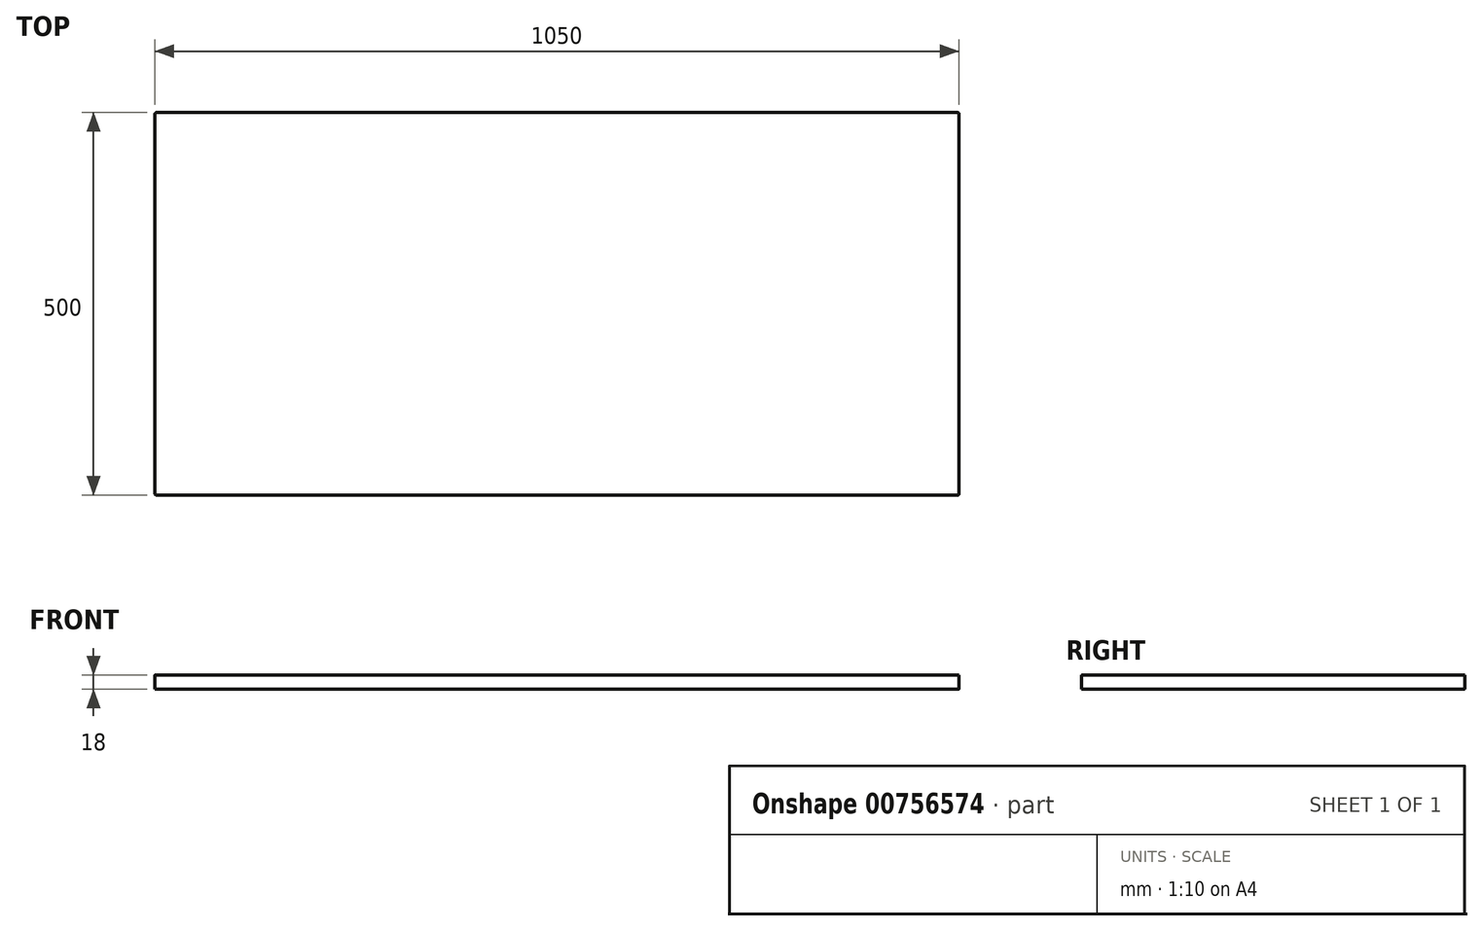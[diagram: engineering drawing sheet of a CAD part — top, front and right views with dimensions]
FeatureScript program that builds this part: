
annotation { "Feature Type Name" : "Feature", "Feature Type Description" : "" }
export const myFeature = defineFeature(function(context is Context, id is Id, definition is map)
    precondition{}
    {
        {
            var Q0;
            Q0=qCreatedBy(makeId("Top.planeOp"),FACE);
            var sketch = newSketch(context, id + "F0", { "sketchPlane" : qUnion([Q0])});
            skLineSegment(sketch, "E0.bottom", {"start": v(2.5, 0) * mm, "end": v(1047.5, 0) * mm});
            skLineSegment(sketch, "E0.top", {"start": v(2.5, 500) * mm, "end": v(1047.5, 500) * mm});
            skLineSegment(sketch, "E0.left", {"start": v(0, 2.5) * mm, "end": v(0, 497.5) * mm});
            skLineSegment(sketch, "E0.right", {"start": v(1050, 2.5) * mm, "end": v(1050, 497.5) * mm});
            skPoint(sketch, "E1.visualSharp", {"position": v(0, 500) * mm});
            skArc(sketch, "E1.filletArc", {"start": v(2.5, 500) * mm, "mid": v(0.73, 499.27) * mm, "end": v(0, 497.5) * mm});
            skPoint(sketch, "E2.visualSharp", {"position": v(0, 0) * mm});
            skArc(sketch, "E2.filletArc", {"start": v(0, 2.5) * mm, "mid": v(0.73, 0.73) * mm, "end": v(2.5, 0) * mm});
            skPoint(sketch, "E3.visualSharp", {"position": v(1050, 500) * mm});
            skArc(sketch, "E3.filletArc", {"start": v(1050, 497.5) * mm, "mid": v(1049.27, 499.27) * mm, "end": v(1047.5, 500) * mm});
            skPoint(sketch, "E4.visualSharp", {"position": v(1050, 0) * mm});
            skArc(sketch, "E4.filletArc", {"start": v(1047.5, 0) * mm, "mid": v(1049.27, 0.73) * mm, "end": v(1050, 2.5) * mm});
            skSolve(sketch);
        }
        {
            var Q0;
            Q0=makeQuery(id+"F0.imprint","IMPRINT",FACE,{"disambiguationData":[TD([[makeQuery(id+"F0.imprint","IMPRINT",EDGE,{"derivedFrom":sQuery(id+"F0.wireOp",EDGE,"E0.bottom")}),1.0]])]});
            extrude(context, id + "F1", {"entities" : qUnion([Q0]), "depth" : 18 * mm, "offsetDistance" : 25 * mm});
        }
    });
